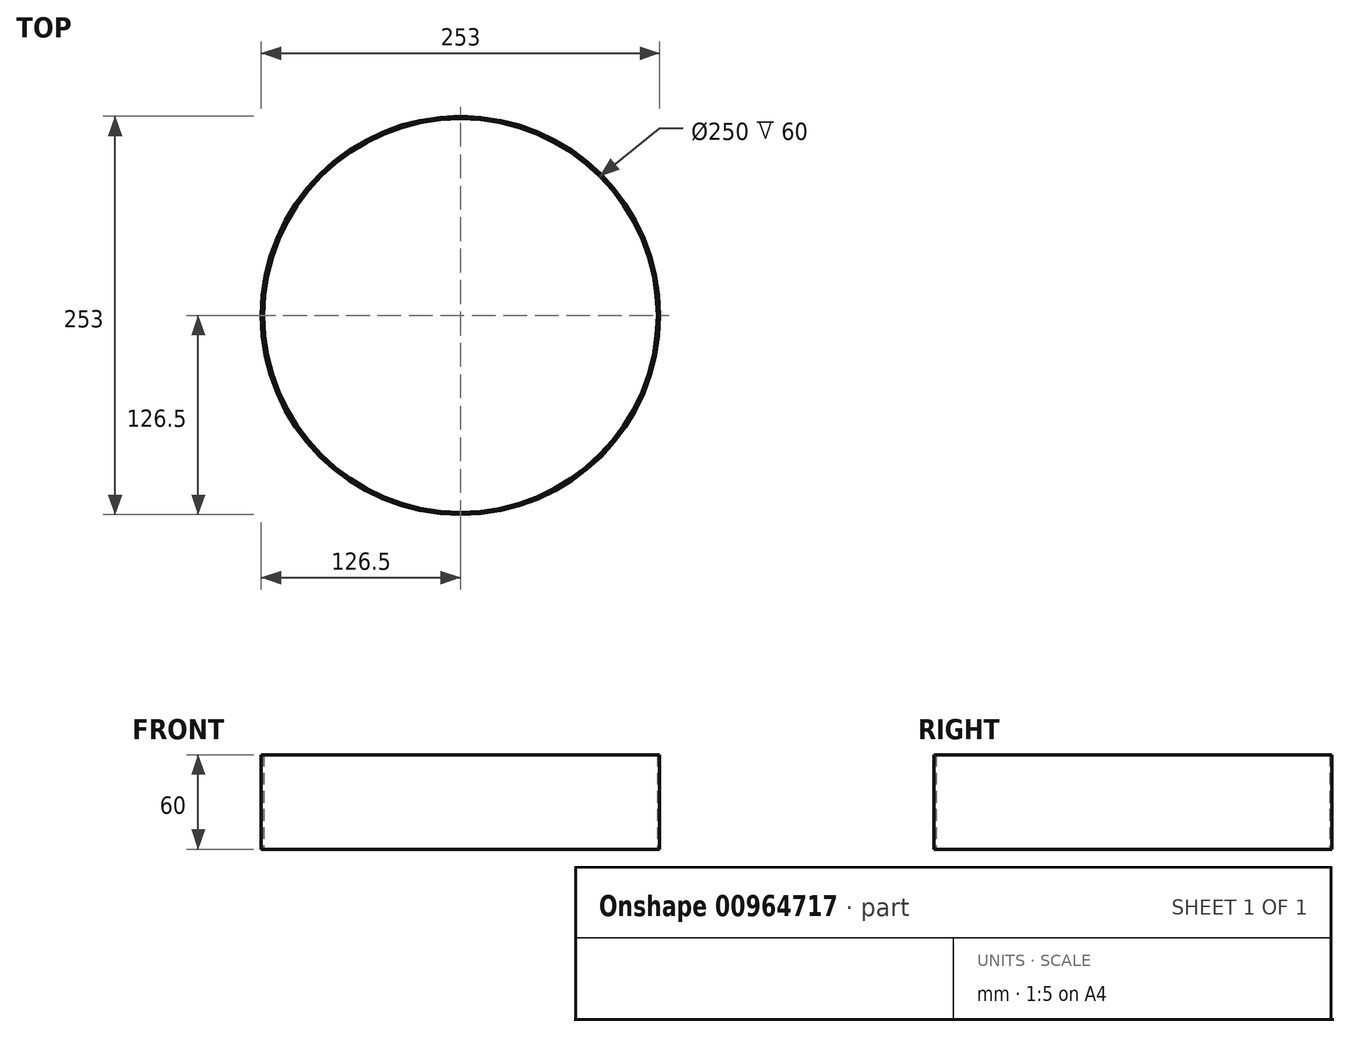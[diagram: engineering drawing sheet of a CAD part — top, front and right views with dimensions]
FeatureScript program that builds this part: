
annotation { "Feature Type Name" : "Feature", "Feature Type Description" : "" }
export const myFeature = defineFeature(function(context is Context, id is Id, definition is map)
    precondition{}
    {
        {
            var Q0;
            Q0=qCreatedBy(makeId("Top.planeOp"), FACE);
            var sketch = newSketch(context, id + "F0", { "sketchPlane" : qUnion([Q0])});
            skCircle(sketch, "E0", {"center": v(0, 0) * mm, "radius": 125 * mm});
            skCircle(sketch, "E1.0", {"center": v(0, 0) * mm, "radius": 126.5 * mm});
            skSolve(sketch);
        }
        {
            var Q0;
            Q0 = qSketchRegion(id + "F0", true);
            extrude(context, id + "F1", {"entities" : qUnion([Q0]), "domain" : OperationDomain.MODEL, "flatOperationType" : FlatOperationType.REMOVE, "depth" : 60 * mm, "offsetDistance" : 25 * mm});
        }
    });
